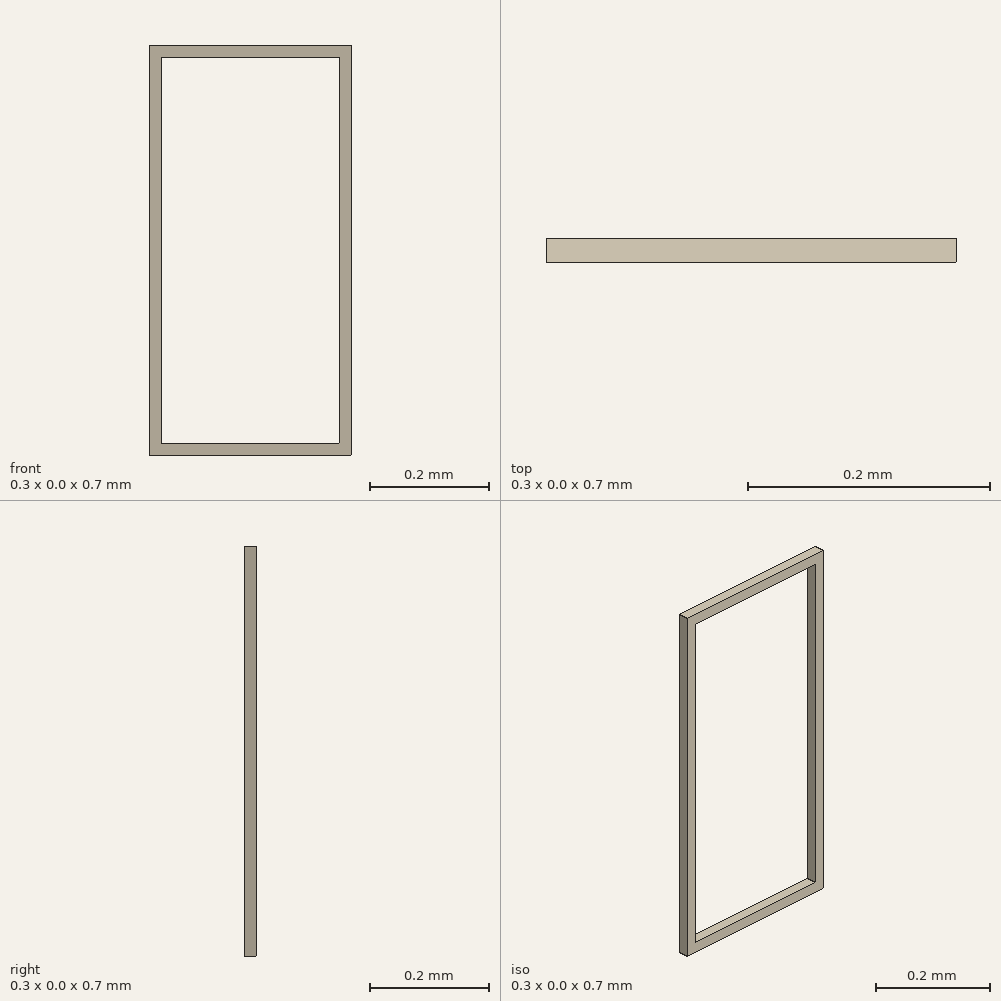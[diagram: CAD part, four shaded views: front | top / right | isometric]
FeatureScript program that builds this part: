
annotation { "Feature Type Name" : "Feature", "Feature Type Description" : "" }
export const myFeature = defineFeature(function(context is Context, id is Id, definition is map)
    precondition{}
    {
        {
            var Q0;
            Q0=qCreatedBy(makeId("Front.planeOp"),FACE);
            var sketch = newSketch(context, id + "F0", { "sketchPlane" : qUnion([Q0])});
            skLineSegment(sketch, "E0.bottom", {"start": v(0.17, 0.34) * mm, "end": v(-0.17, 0.34) * mm});
            skLineSegment(sketch, "E0.top", {"start": v(0.17, -0.34) * mm, "end": v(-0.17, -0.34) * mm});
            skLineSegment(sketch, "E0.left", {"start": v(0.17, 0.35) * mm, "end": v(0.17, -0.34) * mm});
            skLineSegment(sketch, "E0.right", {"start": v(-0.17, 0.35) * mm, "end": v(-0.17, -0.34) * mm});
            skPoint(sketch, "E0.middle", {"position": v(0, 0) * mm});
            skLineSegment(sketch, "E1.bottom", {"start": v(0.15, -0.33) * mm, "end": v(-0.15, -0.33) * mm});
            skLineSegment(sketch, "E1.top", {"start": v(0.15, 0.33) * mm, "end": v(-0.15, 0.33) * mm});
            skLineSegment(sketch, "E1.left", {"start": v(0.15, -0.33) * mm, "end": v(0.15, 0.33) * mm});
            skLineSegment(sketch, "E1.right", {"start": v(-0.15, -0.33) * mm, "end": v(-0.15, 0.33) * mm});
            skSolve(sketch);
        }
        {
            var Q0;
            Q0=makeQuery(id+"F0.imprint","IMPRINT",FACE,{"disambiguationData":[TD([[makeQuery(id+"F0.imprint","IMPRINT",EDGE,{"derivedFrom":sQuery(id+"F0.wireOp",EDGE,"E0.bottom")}),1.0]])]});
            extrude(context, id + "F1", {"entities" : qUnion([Q0]), "depth" : 0.02 * mm});
        }
    });
